# Revit family: 911206003001(architecture=350)
name_source: partatom
category: Plumbing Fixtures
units: mm (PartAtom-declared; Revit-internal decimal feet)

## family parameters
Always vertical = Yes
Cut with Voids When Loaded = No
OmniClass Number = 23.31.13.11
Room Calculation Point = No
Shared = Yes
Work Plane-Based = No

## types (1)
- 911206003001(architecture=350)
    A = 911206003001
    ARTICLENO = NB
    B = kav_nueva.png
    BOMINFO = LINA
    C = NUEVA wash bowl
    CATALOG = Kaldewei
    D = 4.90 kg
    Description = NUEVA wash bowl
    E = KALDEWEI
    EF000007 = White (EV000202)
    EF000049 = 380 mm
    EF000051 = Round (EV000167)
    EF002169 = Steel enamel (EV000166, EV002029)
    EF004567 = 142 mm  [stored 0.465879 ft]
    F = 4055761242721
    H = WEB info
    I = PDF info
    J = all countrys
    K = ISO 14025, EN 15804
    L = 30 Year
    LINA = 911206003001(architecture=350)
    LODLEVEL = 350
    M = Furnishing Element
    Manufacturer = Kaldewei
    Model = 911206003001(architecture=350)
    N = IfcSanitaryTerminalType
    NB = 911206003001(architecture=350)
    NBSYN = $A.($LODDEST.=$LODLEVEL.)
    NN = 911206003001
    NT = NUEVA wash bowl
    O = SS-35-65-70-94
    P = Wash Basin Systems
    Q = 23-31-13-11
    R = RVT_METRICPLUMBINGFIXTURE
    S = EC011550
    SUPPLIER = KALDEWEI
    etim7_EC011550 = EC011550
    ifc40_IFC4_IFCFURNISHINGELEMENT = IFC4_IFCFURNISHINGELEMENT

note: [stored X ft] marks values corroborated as IEEE doubles in the binary element streams (Revit-internal decimal feet)

## geometry (parser evidence)
native form markers: Sweep x4
no freeform markers — native parametric forms only
